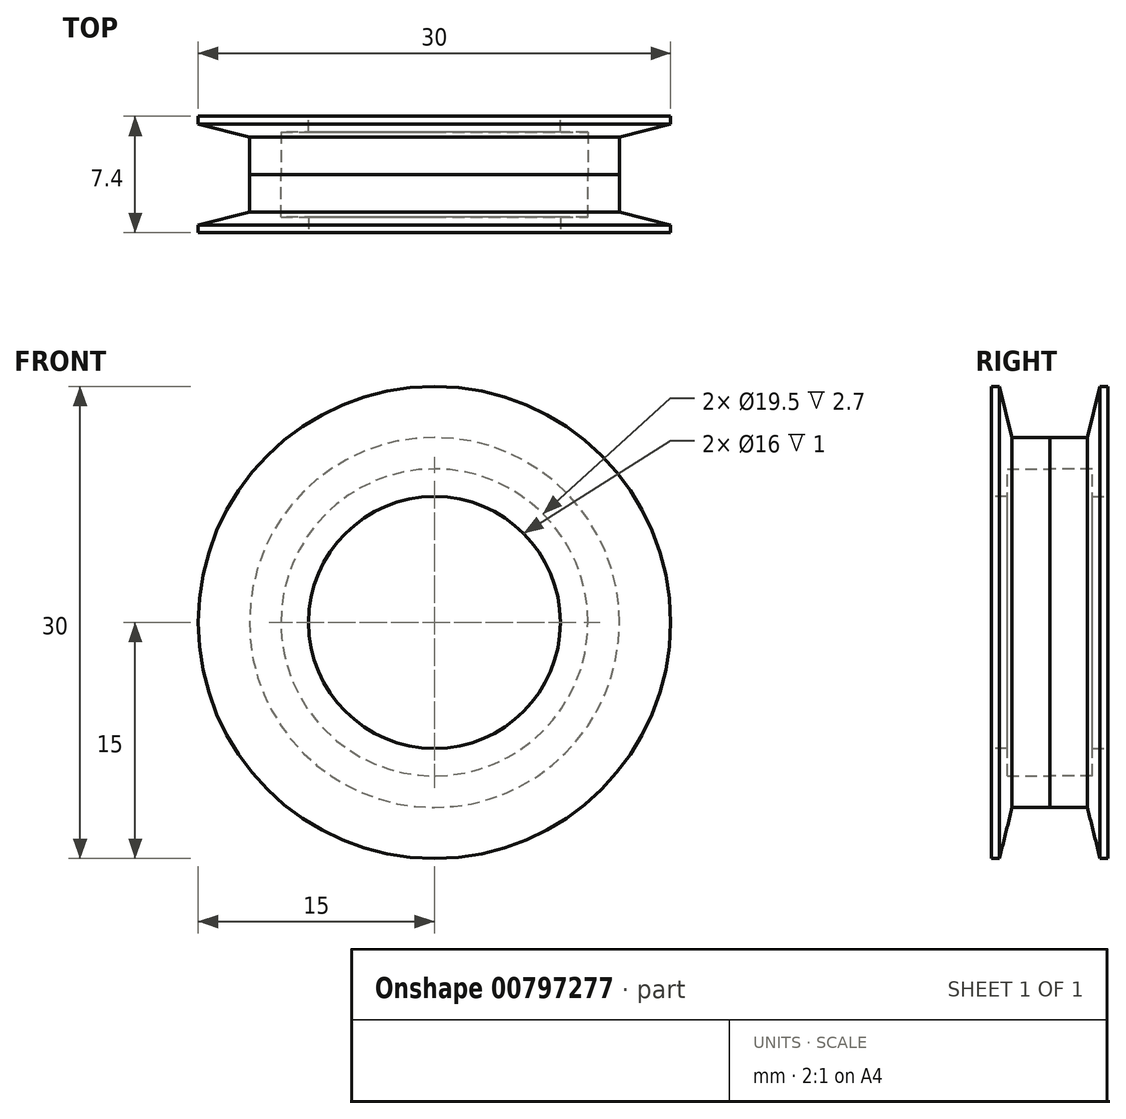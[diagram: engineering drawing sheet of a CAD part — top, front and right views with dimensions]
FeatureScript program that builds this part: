
annotation { "Feature Type Name" : "Feature", "Feature Type Description" : "" }
export const myFeature = defineFeature(function(context is Context, id is Id, definition is map)
    precondition{}
    {
        {
            var Q0;
            Q0=qCreatedBy(makeId("Front.planeOp"),FACE);
            var sketch = newSketch(context, id + "F0", { "sketchPlane" : qUnion([Q0])});
            skCircle(sketch, "E0", {"center": v(0, 0) * mm, "radius": 9.75 * mm});
            skCircle(sketch, "E1.0", {"center": v(0, 0) * mm, "radius": 11.75 * mm});
            skSolve(sketch);
        }
        {
            var Q0;
            Q0=makeQuery(id+"F0.imprint","IMPRINT",FACE,{"disambiguationData":[TD([[makeQuery(id+"F0.imprint","IMPRINT",EDGE,{"derivedFrom":sQuery(id+"F0.wireOp",EDGE,"E0")}),-1.0]])]});
            extrude(context, id + "F1", {"entities" : qUnion([Q0]), "depth" : 1.2 * mm, "offsetDistance" : 25 * mm});
        }
        {
            var Q0;
            Q0=makeQuery(id+"F1.opExtrude","CAP_FACE",FACE,{"disambiguationData":[OSD([sQuery(id+"F0.wireOp",EDGE,"E0"),sQuery(id+"F0.wireOp",EDGE,"E1.0")])],"isStart":false});
            var sketch = newSketch(context, id + "F2", { "sketchPlane" : qUnion([Q0])});
            skCircle(sketch, "E2", {"center": v(0, 0) * mm, "radius": 15 * mm});
            skSolve(sketch);
        }
        {
            var Q0;
            Q0=makeQuery(id+"F2.imprint","IMPRINT",FACE,{"disambiguationData":[TD([[makeQuery(id+"F2.imprint","IMPRINT",EDGE,{"derivedFrom":makeQuery(id+"F1.opExtrude","CAP_EDGE",EDGE,{"disambiguationData":[OSD([sQuery(id+"F0.wireOp",EDGE,"E0")])],"isStart":false})}),-1.0]])]});
            var Q1;
            Q1=makeQuery(id+"F2.imprint","IMPRINT",FACE,{"disambiguationData":[TD([[makeQuery(id+"F2.imprint","IMPRINT",EDGE,{"derivedFrom":sQuery(id+"F2.wireOp",EDGE,"E2")}),1.0]])]});
            extrude(context, id + "F3", {"entities" : qUnion([Q0, Q1]), "operationType" : NewBodyOperationType.ADD, "depth" : 2.5 * mm, "offsetDistance" : 25 * mm});
        }
        {
            var Q0;
            Q0=makeQuery(id+"F3.opExtrude","CAP_EDGE",EDGE,{"disambiguationData":[OSD([sQuery(id+"F2.wireOp",EDGE,"E2")])],"isStart":true});
            chamfer(context, id + "F4", {"entities" : qUnion([Q0]), "chamferType" : ChamferType.TWO_OFFSETS, "width1" : 2 * mm, "oppositeDirection" : false, "width2" : 8 * mm, "tangentPropagation" : true});
        }
        {
            var Q0;
            Q0=makeQuery(id+"F3.opExtrude","CAP_FACE",FACE,{"disambiguationData":[OSD([sQuery(id+"F0.wireOp",EDGE,"E0"),sQuery(id+"F2.wireOp",EDGE,"E2")])],"isStart":false});
            var sketch = newSketch(context, id + "F5", { "sketchPlane" : qUnion([Q0])});
            skCircle(sketch, "E3", {"center": v(0, 0) * mm, "radius": 8 * mm});
            skSolve(sketch);
        }
        {
            var Q0;
            Q0=makeQuery(id+"F5.imprint","IMPRINT",FACE,{"disambiguationData":[TD([[makeQuery(id+"F5.imprint","IMPRINT",EDGE,{"derivedFrom":sQuery(id+"F5.wireOp",EDGE,"E3")}),-1.0]])]});
            extrude(context, id + "F6", {"entities" : qUnion([Q0]), "operationType" : NewBodyOperationType.ADD, "oppositeDirection" : true, "depth" : 1 * mm, "offsetDistance" : 25 * mm});
        }
        {
            var Q0;
            Q0=makeQuery(id+"F1.opExtrude","SWEPT_BODY",BODY,{"disambiguationData":[OSD([sQuery(id+"F0.wireOp",EDGE,"E0"),sQuery(id+"F0.wireOp",EDGE,"E1.0")])]});
            var Q1;
            Q1=makeQuery(id+"F1.opExtrude","CAP_FACE",FACE,{"disambiguationData":[OSD([sQuery(id+"F0.wireOp",EDGE,"E0"),sQuery(id+"F0.wireOp",EDGE,"E1.0")])],"isStart":true});
            mirror(context, id + "F7", {"entities" : qUnion([Q0]), "mirrorPlane" : qUnion([Q1])});
        }
    });
